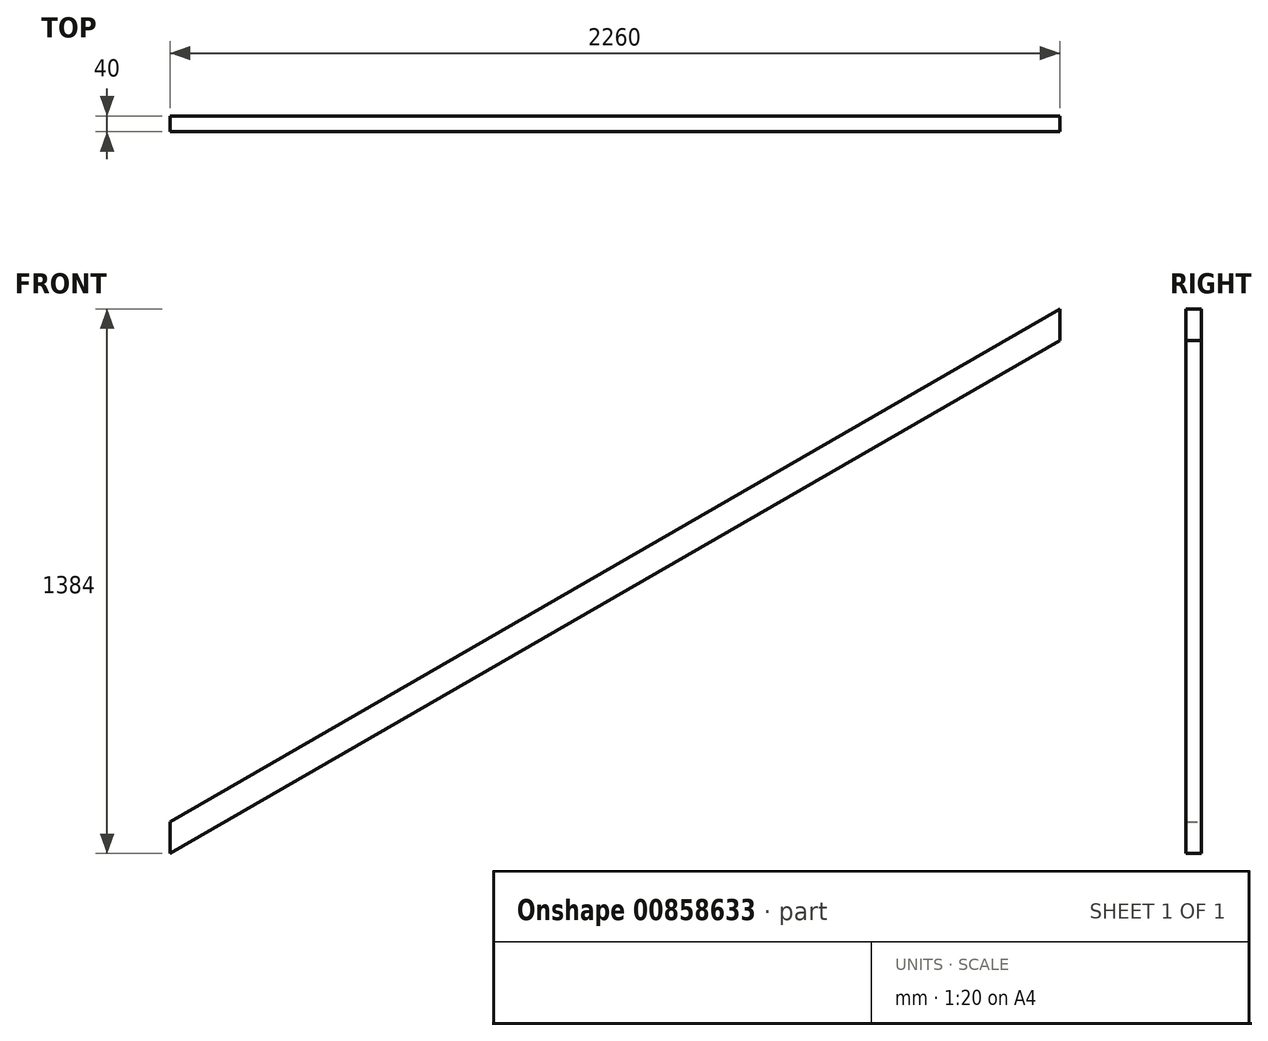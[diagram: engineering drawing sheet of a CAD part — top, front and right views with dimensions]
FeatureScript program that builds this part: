
annotation { "Feature Type Name" : "Feature", "Feature Type Description" : "" }
export const myFeature = defineFeature(function(context is Context, id is Id, definition is map)
    precondition{}
    {
        {
            var Q0;
            Q0=qCreatedBy(makeId("Front.planeOp"),FACE);
            var sketch = newSketch(context, id + "F0", { "sketchPlane" : qUnion([Q0])});
            skLineSegment(sketch, "E0.bottom", {"start": v(1130, 692) * mm, "end": v(-1130, -611.2) * mm});
            skLineSegment(sketch, "E0.top", {"start": v(1130, 611.2) * mm, "end": v(-1130, -692) * mm});
            skLineSegment(sketch, "E0.left", {"start": v(1130, 692) * mm, "end": v(1130, 611.2) * mm});
            skLineSegment(sketch, "E0.right", {"start": v(-1130, -611.2) * mm, "end": v(-1130, -692) * mm});
            skPoint(sketch, "E0.middle", {"position": v(0, 0) * mm});
            skLineSegment(sketch, "E1.top", {"start": v(-1130, 692) * mm, "end": v(1130, 692) * mm, "construction": true});
            skLineSegment(sketch, "E2.bottom", {"start": v(-1130, 692) * mm, "end": v(-1200, 692) * mm, "construction": true});
            skLineSegment(sketch, "E2.top", {"start": v(-1130, -692) * mm, "end": v(-1200, -692) * mm, "construction": true});
            skLineSegment(sketch, "E2.right", {"start": v(-1200, 692) * mm, "end": v(-1200, -692) * mm, "construction": true});
            skLineSegment(sketch, "E3.bottom", {"start": v(1130, 692) * mm, "end": v(1200, 692) * mm, "construction": true});
            skLineSegment(sketch, "E3.top", {"start": v(1130, -692) * mm, "end": v(1200, -692) * mm, "construction": true});
            skLineSegment(sketch, "E3.right", {"start": v(1200, 692) * mm, "end": v(1200, -692) * mm, "construction": true});
            skLineSegment(sketch, "E4.top", {"start": v(-1200, 762) * mm, "end": v(1200, 762) * mm, "construction": true});
            skLineSegment(sketch, "E4.left", {"start": v(-1200, 692) * mm, "end": v(-1200, 762) * mm, "construction": true});
            skLineSegment(sketch, "E4.right", {"start": v(1200, 692) * mm, "end": v(1200, 762) * mm, "construction": true});
            skLineSegment(sketch, "E5.bottom", {"start": v(-1200, -692) * mm, "end": v(1200, -692) * mm, "construction": true});
            skLineSegment(sketch, "E5.top", {"start": v(-1200, -762) * mm, "end": v(1200, -762) * mm, "construction": true});
            skLineSegment(sketch, "E5.left", {"start": v(-1200, -692) * mm, "end": v(-1200, -762) * mm, "construction": true});
            skLineSegment(sketch, "E5.right", {"start": v(1200, -692) * mm, "end": v(1200, -762) * mm, "construction": true});
            skLineSegment(sketch, "E6.top", {"start": v(-1200, -782) * mm, "end": v(1200, -782) * mm, "construction": true});
            skLineSegment(sketch, "E6.left", {"start": v(-1200, -762) * mm, "end": v(-1200, -782) * mm, "construction": true});
            skLineSegment(sketch, "E6.right", {"start": v(1200, -762) * mm, "end": v(1200, -782) * mm, "construction": true});
            skLineSegment(sketch, "E7", {"start": v(-1130, 692) * mm, "end": v(-1130, -611.2) * mm, "construction": true});
            skLineSegment(sketch, "E8", {"start": v(1130, 611.2) * mm, "end": v(1130, -692) * mm, "construction": true});
            skSolve(sketch);
        }
        {
            var Q0;
            Q0 = qSketchRegion(id + "F0", true);
            extrude(context, id + "F1", {"entities" : qUnion([Q0]), "endBound" : BoundingType.SYMMETRIC, "depth" : 40 * mm, "offsetDistance" : 25 * mm});
        }
    });
